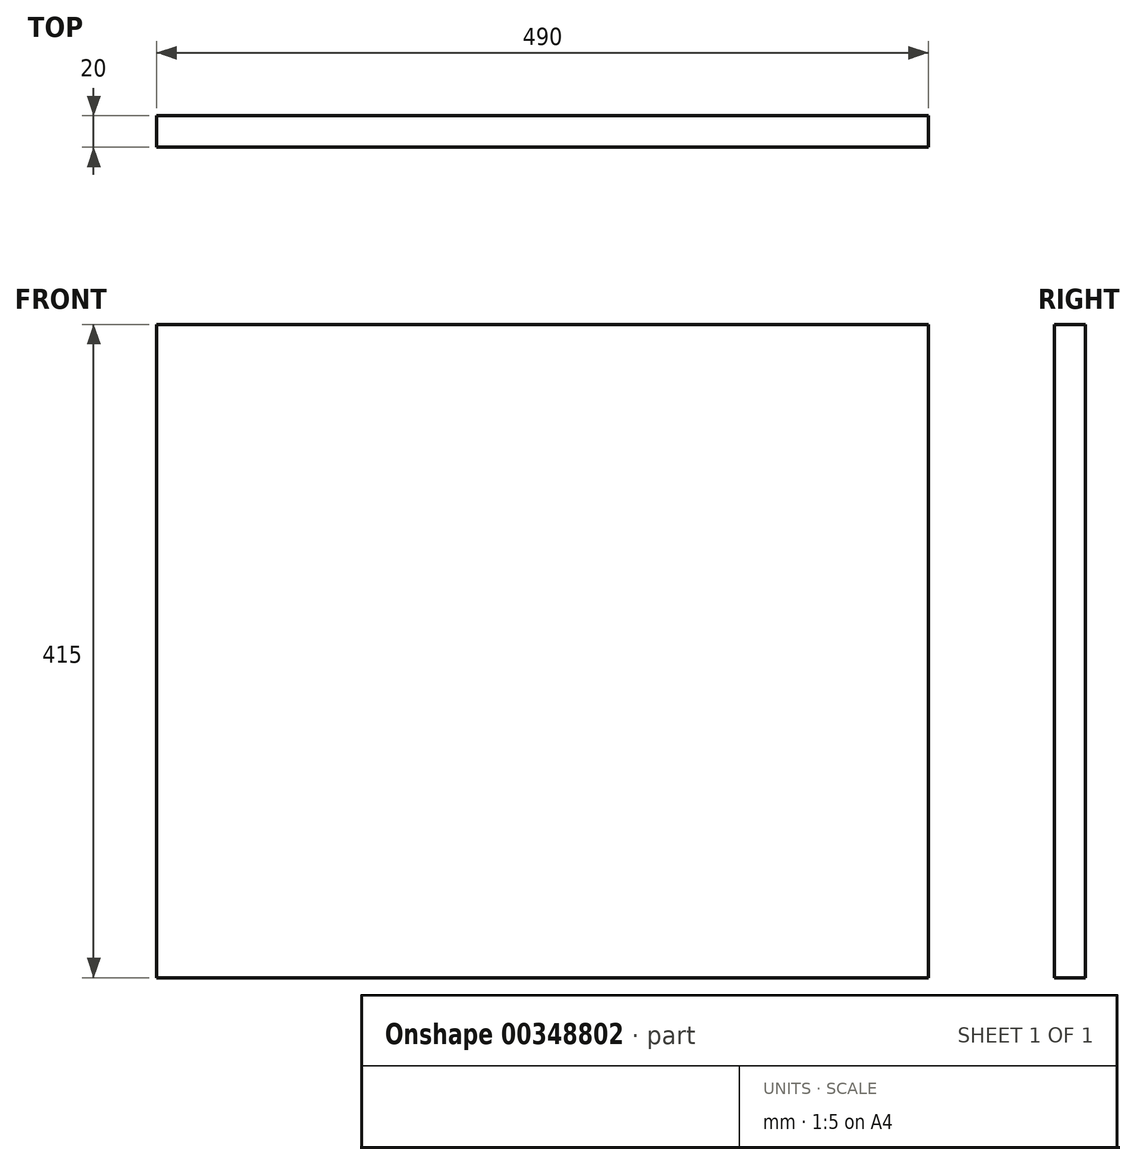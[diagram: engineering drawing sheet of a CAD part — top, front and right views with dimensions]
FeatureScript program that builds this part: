
annotation { "Feature Type Name" : "Feature", "Feature Type Description" : "" }
export const myFeature = defineFeature(function(context is Context, id is Id, definition is map)
    precondition{}
    {
        {
            var Q0;
            Q0=qCreatedBy(makeId("Front.planeOp"),FACE);
            var sketch = newSketch(context, id + "F0", { "sketchPlane" : qUnion([Q0])});
            skLineSegment(sketch, "E0.bottom", {"start": v(-490, -415) * mm, "end": v(0, -415) * mm});
            skLineSegment(sketch, "E0.top", {"start": v(-490, 0) * mm, "end": v(0, 0) * mm});
            skLineSegment(sketch, "E0.left", {"start": v(-490, -415) * mm, "end": v(-490, 0) * mm});
            skLineSegment(sketch, "E0.right", {"start": v(0, -415) * mm, "end": v(0, 0) * mm});
            skSolve(sketch);
        }
        {
            var Q0;
            Q0=qSketchRegion(id+"F0",true);
            extrude(context, id + "F1", {"entities" : qUnion([Q0]), "depth" : 20 * mm});
        }
    });
